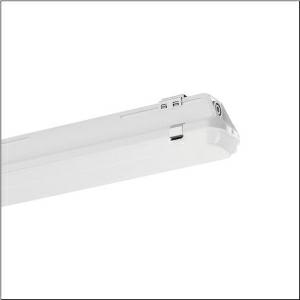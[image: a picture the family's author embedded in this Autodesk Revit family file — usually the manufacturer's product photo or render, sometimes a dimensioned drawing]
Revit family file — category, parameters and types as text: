
# Revit family: monsun_r__11_facade_51ff40mp460h_34d2
name_source: partatom
category: Lighting Fixtures
units: mm (PartAtom-declared; Revit-internal decimal feet)

## family parameters
Cut with Voids When Loaded = No
Host = Face
Light Source = No
Part Type = Normal
Room Calculation Point = No
Round Connector Dimension = Use Diameter
Shared = No

## types (1)
- --- (1 x LED, 6110 lm, 33.5 W, 4000K)
    Apparent Load = 34 VA
    CIE Flux Codes = 47 77 93 95 100
    Color Rendering = 80
    Color Temperature = 4000K
    Default Elevation = 1800 mm
    Description = Monsun® 11 facade, damp-proof luminaire, chain hanger, primary optical cover: enclosure, of PMMA, light emission: direct distribution, primary light characteristic: symmetric, installation type: surface-mounted, horizontal mounting, vertical mounting, LED, rated luminous flux: 6.110lm, luminous efficacy: 182lm/W, light colour: 840, colour temperature: 4000K, control gear: ON/OFF Multilumen, with terminal, 3-pole, max. 2.5mm², mains connection: 220..240V, AC, 50/60Hz, rated input power: 34W, luminaire housing, of glass-fibre reinforced polyester, uncoated, bright grey, incl. chain hanger, for cables, Ø 8.4..12mm, with climate membrane, length: 1.590mm, width: 90mm, height: 88mm, clip for enclosure, of stainless steel (V2A), ceiling mounting element, of stainless steel (V2A), chain hanger, of stainless steel (V2A), protection rating (complete): IP66, insulation class (complete): insulation class I (protective earthing), certification: CE, ENEC, VDE, UKCA, protection symbol: D, impact resistance: IK06, permissible operating ambient temperature: -35..+50°C, standard: EN 50419, EN 60598-2-1, contact your sales advisor before using the luminaires in applications with unclear chemical exposure, large temperature fluctuations or condensation-forming humidity, LABS conformity tested according to VDMA 24364:2018-05, exposed outdoor area, packaging unit: 1 piece
    Height = 89 mm
    Lamp = 1 x LED
    Lamp Light Flux = 6110 lm
    Lamp Power = 33.5 W
    Lamp count = 1
    Length = 1590 mm
    Luminous efficacy = 182 lm/W
    Manufacturer = Siteco
    ModVariant = No
    Model = 51FF40MP460H
    Mounting Place = Ceiling
    Mounting Type = Surface mounted
    Number of Poles = 1
    OnlyDefault = Yes
    Power Factor = 1
    Product Name = Monsun® 11 facade
    Product group = damp-proof luminaire
    ProductGroupID = 301
    Protection Class = Protection class I
    Protection Degree = IP 66
    RLX_Detail_Level = 1
    RLX_Emergency_Light_Flux = 0 lm
    RLX_Emergency_Type = 0
    RLX_Emergency_Type_DB = No
    RlxData = <blob elided: 89917 chars, md5=667ec56f>
    Socket = socket
    Standby Power = 0 W
    System Light Flux = 6110 lm
    System Power = 34 W
    Type Comments = factory setting: luminous flux: 100 % | (A | C | E) | 77 mA
    Type Image = l_1349237.jpg
    URL = http://relux.com
    VarID = @adj_219731
    Voltage = 0 V
    Weight = 0.00 kg
    Width = 90 mm

## geometry (parser evidence)
native form markers: Blend x4, Sweep x13
no freeform markers — native parametric forms only
